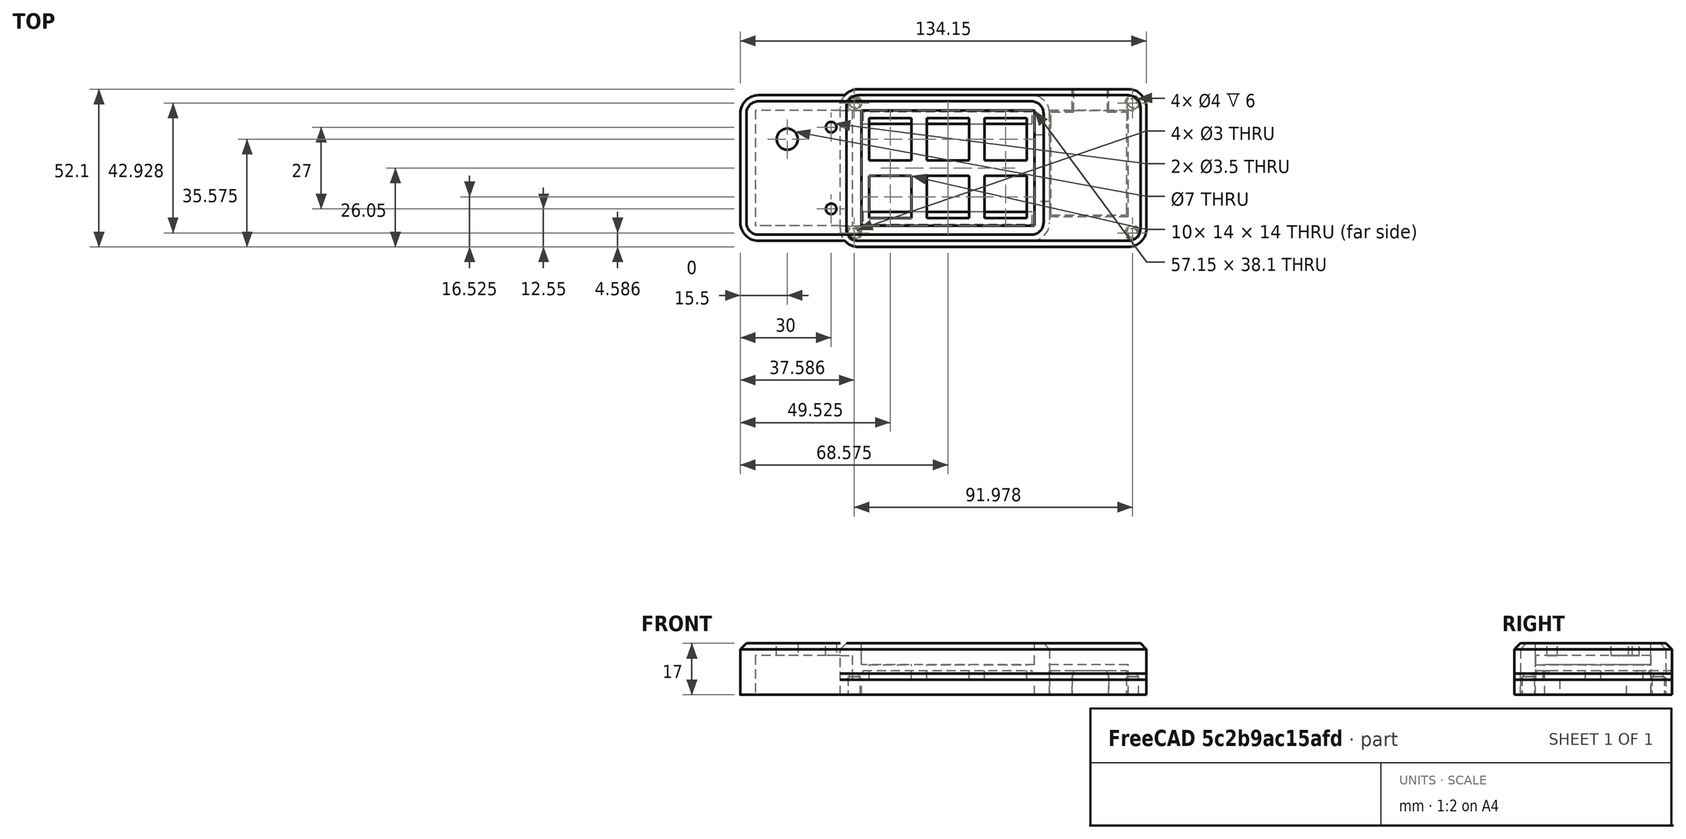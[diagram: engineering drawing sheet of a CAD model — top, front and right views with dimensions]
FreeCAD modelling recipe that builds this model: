
FCSTD DOCUMENT  (FreeCAD 0.21RUnknown)
Label: tm_keyb
License: All rights reserved
LicenseURL: https://en.wikipedia.org/wiki/All_rights_reserved
objects: Sketcher::SketchObject×18, TechDraw::DrawViewDimension×18, PartDesign::Pad×11, PartDesign::Pocket×9, TechDraw::DrawViewPart×6, PartDesign::Fillet×3, PartDesign::Chamfer×3, PartDesign::Body×3, PartDesign::ShapeBinder×1, Part::Mirroring×1, TechDraw::DrawSVGTemplate×1, TechDraw::DrawPage×1
note: 103 computed .brp shape members not serialized (recipe doc carries the construction recipe); baked Part::Feature solids carry a one-line shape summary decoded from their .brp

FEATURE [Sketcher::SketchObject] Sketch
  FullyConstrained = true
  MapMode = 5
  Support = -> [XY_Plane]
  sketch-geometry (45):
    g0: LineSegment StartX=-57.15 StartY=38.1 StartZ=0 EndX=0 EndY=38.1 EndZ=0
    g1: LineSegment StartX=0 StartY=38.1 StartZ=0 EndX=0 EndY=0 EndZ=0
    g2: LineSegment StartX=0 StartY=0 StartZ=0 EndX=-57.15 EndY=0 EndZ=0
    g3: LineSegment StartX=-57.15 StartY=0 StartZ=0 EndX=-57.15 EndY=38.1 EndZ=0
    g4: LineSegment StartX=-54.625 StartY=35.575 StartZ=0 EndX=-40.625 EndY=35.575 EndZ=0
    g5: LineSegment StartX=-40.625 StartY=35.575 StartZ=0 EndX=-40.625 EndY=21.575 EndZ=0
    g6: LineSegment StartX=-40.625 StartY=21.575 StartZ=0 EndX=-54.625 EndY=21.575 EndZ=0
    g7: LineSegment StartX=-54.625 StartY=21.575 StartZ=0 EndX=-54.625 EndY=35.575 EndZ=0
    g8: LineSegment StartX=-35.575 StartY=35.575 StartZ=0 EndX=-21.575 EndY=35.575 EndZ=0
    g9: LineSegment StartX=-21.575 StartY=35.575 StartZ=0 EndX=-21.575 EndY=21.575 EndZ=0
    g10: LineSegment StartX=-21.575 StartY=21.575 StartZ=0 EndX=-35.575 EndY=21.575 EndZ=0
    g11: LineSegment StartX=-35.575 StartY=21.575 StartZ=0 EndX=-35.575 EndY=35.575 EndZ=0
    g12: LineSegment StartX=-16.525 StartY=35.575 StartZ=0 EndX=-2.525 EndY=35.575 EndZ=0
    g13: LineSegment StartX=-2.525 StartY=35.575 StartZ=0 EndX=-2.525 EndY=21.575 EndZ=0
    g14: LineSegment StartX=-2.525 StartY=21.575 StartZ=0 EndX=-16.525 EndY=21.575 EndZ=0
    g15: LineSegment StartX=-16.525 StartY=21.575 StartZ=0 EndX=-16.525 EndY=35.575 EndZ=0
    g16: LineSegment StartX=-54.625 StartY=16.525 StartZ=0 EndX=-40.625 EndY=16.525 EndZ=0
    g17: LineSegment StartX=-40.625 StartY=16.525 StartZ=0 EndX=-40.625 EndY=2.525 EndZ=0
    g18: LineSegment StartX=-40.625 StartY=2.525 StartZ=0 EndX=-54.625 EndY=2.525 EndZ=0
    g19: LineSegment StartX=-54.625 StartY=2.525 StartZ=0 EndX=-54.625 EndY=16.525 EndZ=0
    g20: LineSegment StartX=-35.575 StartY=16.525 StartZ=0 EndX=-21.575 EndY=16.525 EndZ=0
    g21: LineSegment StartX=-21.575 StartY=16.525 StartZ=0 EndX=-21.575 EndY=2.525 EndZ=0
    g22: LineSegment StartX=-21.575 StartY=2.525 StartZ=0 EndX=-35.575 EndY=2.525 EndZ=0
    g23: LineSegment StartX=-35.575 StartY=2.525 StartZ=0 EndX=-35.575 EndY=16.525 EndZ=0
    g24: LineSegment StartX=-16.525 StartY=16.525 StartZ=0 EndX=-2.525 EndY=16.525 EndZ=0
    g25: LineSegment StartX=-2.525 StartY=16.525 StartZ=0 EndX=-2.525 EndY=2.525 EndZ=0
    g26: LineSegment StartX=-2.525 StartY=2.525 StartZ=0 EndX=-16.525 EndY=2.525 EndZ=0
    g27: LineSegment StartX=-16.525 StartY=2.525 StartZ=0 EndX=-16.525 EndY=16.525 EndZ=0
    g28: LineSegment StartX=0 StartY=38.1 StartZ=0 EndX=-19.05 EndY=38.1 EndZ=0
    g29: LineSegment StartX=-19.05 StartY=38.1 StartZ=0 EndX=-19.05 EndY=19.05 EndZ=0
    g30: LineSegment StartX=-19.05 StartY=19.05 StartZ=0 EndX=0 EndY=19.05 EndZ=0
    g31: LineSegment StartX=0 StartY=19.05 StartZ=0 EndX=0 EndY=38.1 EndZ=0
    g32: LineSegment StartX=-16.525 StartY=35.575 StartZ=0 EndX=-19.05 EndY=38.1 EndZ=0
    g33: LineSegment StartX=-2.525 StartY=35.575 StartZ=0 EndX=0 EndY=38.1 EndZ=0
    g34: LineSegment StartX=-2.525 StartY=21.575 StartZ=0 EndX=0 EndY=19.05 EndZ=0
    g35: LineSegment StartX=-16.525 StartY=21.575 StartZ=0 EndX=-19.05 EndY=19.05 EndZ=0
    g36: LineSegment StartX=-57.15 StartY=19.05 StartZ=0 EndX=-38.1 EndY=19.05 EndZ=0
    g37: LineSegment StartX=-38.1 StartY=19.05 StartZ=0 EndX=-38.1 EndY=0 EndZ=0
    g38: LineSegment StartX=-38.1 StartY=0 StartZ=0 EndX=-57.15 EndY=0 EndZ=0
    g39: LineSegment StartX=-57.15 StartY=0 StartZ=0 EndX=-57.15 EndY=19.05 EndZ=0
    g40: LineSegment StartX=-19.05 StartY=19.05 StartZ=0 EndX=0 EndY=19.05 EndZ=0
    g41: LineSegment StartX=0 StartY=19.05 StartZ=0 EndX=0 EndY=0 EndZ=0
    g42: LineSegment StartX=0 StartY=0 StartZ=0 EndX=-19.05 EndY=0 EndZ=0
    g43: LineSegment StartX=-19.05 StartY=0 StartZ=0 EndX=-19.05 EndY=19.05 EndZ=0
    g44: LineSegment StartX=-38.1 StartY=19.05 StartZ=0 EndX=-19.05 EndY=19.05 EndZ=0
  constraints (126):
    c: Coincident(g0,g1)
    c: Coincident(g1,g2)
    c: Coincident(g2,g3)
    c: Coincident(g3,g0)
    c: Horizontal(g0)
    c: Horizontal(g2)
    c: Vertical(g1)
    c: Vertical(g3)
    c: Coincident(g1,g-1)
    c: Coincident(g4,g5)
    c: Coincident(g5,g6)
    c: Coincident(g6,g7)
    c: Coincident(g7,g4)
    c: Horizontal(g4)
    c: Horizontal(g6)
    c: Vertical(g5)
    c: Vertical(g7)
    c: Coincident(g8,g9)
    c: Coincident(g9,g10)
    c: Coincident(g10,g11)
    c: Coincident(g11,g8)
    c: Horizontal(g8)
    c: Horizontal(g10)
    c: Vertical(g9)
    c: Vertical(g11)
    c: Coincident(g12,g13)
    c: Coincident(g13,g14)
    c: Coincident(g14,g15)
    c: Coincident(g15,g12)
    c: Horizontal(g12)
    c: Horizontal(g14)
    c: Vertical(g13)
    c: Vertical(g15)
    c: Coincident(g16,g17)
    c: Coincident(g17,g18)
    c: Coincident(g18,g19)
    c: Coincident(g19,g16)
    c: Horizontal(g16)
    c: Horizontal(g18)
    c: Vertical(g17)
    c: Vertical(g19)
    c: Coincident(g20,g21)
    c: Coincident(g21,g22)
    c: Coincident(g22,g23)
    c: Coincident(g23,g20)
    c: Horizontal(g20)
    c: Horizontal(g22)
    c: Vertical(g21)
    c: Vertical(g23)
    c: Coincident(g24,g25)
    c: Coincident(g25,g26)
    c: Coincident(g26,g27)
    c: Coincident(g27,g24)
    c: Horizontal(g24)
    c: Horizontal(g26)
    c: Vertical(g25)
    c: Vertical(g27)
    c: Horizontal(g10,g5)
    c: Horizontal(g5,g14)
    c: Horizontal(g16,g20)
    c: Horizontal(g20,g24)
    c: Vertical(g20,g10)
    c: Vertical(g5,g16)
    c: Vertical(g24,g14)
    c: Equal(g15,g12)
    c: Equal(g12,g8)
    c: Equal(g8,g9)
    c: Equal(g9,g4)
    c: Equal(g4,g5)
    c: Equal(g5,g16)
    c: Equal(g16,g17)
    c: Equal(g17,g24)
    c: Equal(g24,g27)
    c: Equal(g27,g21)
    c: Equal(g21,g20)
    c: DistanceX(g4,g4) = 14
    c: DistanceX(g4,g8) = 5.05
    c: DistanceX(g8,g12) = 5.05
    c: DistanceY(g24,g13) = 5.05
    c: Coincident(g28,g29)
    c: Coincident(g29,g30)
    c: Coincident(g30,g31)
    c: Coincident(g31,g28)
    c: Horizontal(g28)
    c: Horizontal(g30)
    c: Vertical(g29)
    c: Vertical(g31)
    c: Equal(g28,g31)
    c: DistanceY(g31,g31) = 19.05
    c: Coincident(g32,g12)
    c: Coincident(g32,g28)
    c: Coincident(g33,g12)
    c: Coincident(g33,g28)
    c: Coincident(g34,g13)
    c: Coincident(g34,g30)
    c: Coincident(g35,g14)
    c: Coincident(g35,g29)
    c: Equal(g35,g34)
    c: Equal(g34,g33)
    c: Vertical(g30,g1)
    c: Coincident(g36,g37)
    c: Coincident(g37,g38)
    c: Coincident(g38,g39)
    c: Coincident(g39,g36)
    c: Horizontal(g36)
    c: Horizontal(g38)
    c: Vertical(g37)
    c: Vertical(g39)
    c: PointOnObject(g37,g2)
    c: Coincident(g40,g41)
    c: Coincident(g41,g42)
    c: Coincident(g42,g43)
    c: Coincident(g43,g40)
    c: Horizontal(g42)
    c: Vertical(g43)
    c: Coincident(g40,g29)
    c: Coincident(g40,g30)
    c: Coincident(g41,g1)
    c: Equal(g29,g43)
    c: Equal(g43,g36)
    c: Equal(g36,g37)
    c: Coincident(g44,g36)
    c: Coincident(g44,g29)
    c: Equal(g44,g36)
    c: Vertical(g36,g0)
    c: Horizontal(g0,g28)
FEATURE [PartDesign::Pad] Pad
  Direction = (0,0,1)
  Length = 5
  Length2 = 10
  Profile = -> Sketch
  ReferenceAxis = -> Sketch [N_Axis]
  Type = 0
FEATURE [Sketcher::SketchObject] Sketch001
  ExternalGeometry = -> [Pad]
  FullyConstrained = true
  MapMode = 5
  Support = -> [XY_Plane]
  sketch-geometry (8):
    g0: LineSegment StartX=-64.15 StartY=45.1 StartZ=0 EndX=7 EndY=45.1 EndZ=0
    g1: LineSegment StartX=7 StartY=45.1 StartZ=0 EndX=7 EndY=-7 EndZ=0
    g2: LineSegment StartX=7 StartY=-7 StartZ=0 EndX=-64.15 EndY=-7 EndZ=0
    g3: LineSegment StartX=-64.15 StartY=-7 StartZ=0 EndX=-64.15 EndY=45.1 EndZ=0
    g4: LineSegment StartX=-57.15 StartY=38.1 StartZ=0 EndX=0 EndY=38.1 EndZ=0
    g5: LineSegment StartX=0 StartY=38.1 StartZ=0 EndX=0 EndY=0 EndZ=0
    g6: LineSegment StartX=0 StartY=0 StartZ=0 EndX=-57.15 EndY=0 EndZ=0
    g7: LineSegment StartX=-57.15 StartY=0 StartZ=0 EndX=-57.15 EndY=38.1 EndZ=0
  constraints (22):
    c: Coincident(g0,g1)
    c: Coincident(g1,g2)
    c: Coincident(g2,g3)
    c: Coincident(g3,g0)
    c: Horizontal(g0)
    c: Horizontal(g2)
    c: Vertical(g1)
    c: Vertical(g3)
    c: Coincident(g4,g5)
    c: Coincident(g5,g6)
    c: Coincident(g6,g7)
    c: Coincident(g7,g4)
    c: Horizontal(g4)
    c: Horizontal(g6)
    c: Vertical(g5)
    c: Vertical(g7)
    c: Coincident(g5,g-1)
    c: Coincident(g4,g-3)
    c: DistanceX(g0,g4) = 7
    c: DistanceX(g4,g0) = 7
    c: DistanceY(g1,g5) = 7
    c: DistanceY(g4,g0) = 7
FEATURE [PartDesign::Pad] Pad001
  BaseFeature = -> Pad
  Direction = (0,0,1)
  Length = 12
  Length2 = 5
  Profile = -> Sketch001
  ReferenceAxis = -> Sketch001 [N_Axis]
  Type = 4
  expr: Length = 5 + 7
FEATURE [Sketcher::SketchObject] Sketch002
  ExternalGeometry = -> [Pad001]
  FullyConstrained = true
  MapMode = 5
  Placement = pos=(-64.15,0,0) rot=(0.57735,-0.57735,-0.57735;2.0944rad)
  Support = -> [Pad001]
  sketch-geometry (4):
    g0: LineSegment StartX=-45.1 StartY=12 StartZ=0 EndX=7 EndY=12 EndZ=0
    g1: LineSegment StartX=7 StartY=12 StartZ=0 EndX=7 EndY=8 EndZ=0
    g2: LineSegment StartX=7 StartY=8 StartZ=0 EndX=-45.1 EndY=8 EndZ=0
    g3: LineSegment StartX=-45.1 StartY=8 StartZ=0 EndX=-45.1 EndY=12 EndZ=0
  constraints (10):
    c: Coincident(g0,g1)
    c: Coincident(g1,g2)
    c: Coincident(g2,g3)
    c: Coincident(g3,g0)
    c: Horizontal(g2)
    c: Vertical(g1)
    c: Vertical(g3)
    c: Coincident(g-3,g0)
    c: Coincident(g0,g-3)
    c: DistanceY(g1,g1) = 4
FEATURE [PartDesign::Pad] Pad002
  BaseFeature = -> Pad001
  Direction = (-1,0,0)
  Length = 35
  Length2 = 10
  Profile = -> Sketch002
  ReferenceAxis = -> Sketch002 [N_Axis]
  Type = 0
FEATURE [Sketcher::SketchObject] Sketch003
  ExternalGeometry = -> [Pad002]
  FullyConstrained = true
  MapMode = 5
  Placement = pos=(0,0,12) rot=(0,0,1;0rad)
  Support = -> [Pad002]
  sketch-geometry (5):
    g0: Circle CenterX=-81.65 CenterY=28.575 CenterZ=0 NormalX=0 NormalY=0 NormalZ=1 AngleXU=0 Radius=3.5
    g1: LineSegment StartX=-99.15 StartY=45.1 StartZ=0 EndX=-81.65 EndY=28.575 EndZ=0
    g2: LineSegment StartX=-81.65 StartY=28.575 StartZ=0 EndX=-64.15 EndY=45.1 EndZ=0
    g3: LineSegment StartX=-81.65 StartY=28.575 StartZ=0 EndX=-54.625 EndY=35.575 EndZ=0
    g4: LineSegment StartX=-81.65 StartY=28.575 StartZ=0 EndX=-54.625 EndY=21.575 EndZ=0
  constraints (11):
    c: Diameter(g0) = 7
    c: Coincident(g1,g-3)
    c: Coincident(g1,g0)
    c: Coincident(g2,g0)
    c: Coincident(g2,g-4)
    c: Equal(g2,g1)
    c: Coincident(g3,g0)
    c: Coincident(g3,g-5)
    c: Coincident(g4,g0)
    c: Coincident(g4,g-5)
    c: Equal(g3,g4)
FEATURE [PartDesign::Pocket] Pocket
  BaseFeature = -> Pad002
  Direction = (0,0,-1)
  Length = 5
  Length2 = 5
  Profile = -> Sketch003
  ReferenceAxis = -> Sketch003 [N_Axis]
  Type = 1
FEATURE [Sketcher::SketchObject] Sketch004
  ExternalGeometry = -> [Pocket]
  FullyConstrained = true
  MapMode = 5
  Placement = pos=(-64.15,0,0) rot=(0.57735,-0.57735,-0.57735;2.0944rad)
  Support = -> [Pocket]
  sketch-geometry (4):
    g0: LineSegment StartX=-38.1 StartY=-5 StartZ=0 EndX=0 EndY=-5 EndZ=0
    g1: LineSegment StartX=0 StartY=-5 StartZ=0 EndX=0 EndY=8 EndZ=0
    g2: LineSegment StartX=0 StartY=8 StartZ=0 EndX=-38.1 EndY=8 EndZ=0
    g3: LineSegment StartX=-38.1 StartY=8 StartZ=0 EndX=-38.1 EndY=-5 EndZ=0
  constraints (10):
    c: Coincident(g0,g1)
    c: Coincident(g1,g2)
    c: Coincident(g2,g3)
    c: Coincident(g3,g0)
    c: Horizontal(g2)
    c: Vertical(g1)
    c: Vertical(g3)
    c: Coincident(g0,g-3)
    c: PointOnObject(g1,g-5)
    c: Coincident(g0,g-4)
FEATURE [PartDesign::Pocket] Pocket001
  BaseFeature = -> Pocket
  Direction = (1,0,0)
  Length = 7
  Length2 = 5
  Profile = -> Sketch004
  ReferenceAxis = -> Sketch004 [N_Axis]
  Type = 0
FEATURE [PartDesign::Pad] Pad003
  BaseFeature = -> Pocket001
  Direction = (-1,0,0)
  Length = 10
  Length2 = 10
  Profile = -> Pocket001 [Face2,Face12]
  Type = 3
  UpToFace = -> Pocket001 [Face10]
FEATURE [Sketcher::SketchObject] Sketch005
  ExternalGeometry = -> [Pad003]
  FullyConstrained = true
  MapMode = 5
  Placement = pos=(0,38.1,0) rot=(1,0,0;1.5708rad)
  Support = -> [Pad003]
  sketch-geometry (4):
    g0: LineSegment StartX=-99.15 StartY=8 StartZ=0 EndX=-92.15 EndY=8 EndZ=0
    g1: LineSegment StartX=-92.15 StartY=8 StartZ=0 EndX=-92.15 EndY=-5 EndZ=0
    g2: LineSegment StartX=-92.15 StartY=-5 StartZ=0 EndX=-99.15 EndY=-5 EndZ=0
    g3: LineSegment StartX=-99.15 StartY=-5 StartZ=0 EndX=-99.15 EndY=8 EndZ=0
  constraints (10):
    c: Coincident(g0,g1)
    c: Coincident(g1,g2)
    c: Coincident(g2,g3)
    c: Coincident(g3,g0)
    c: Horizontal(g0)
    c: Horizontal(g2)
    c: Vertical(g1)
    c: DistanceX(g2,g2) = 7
    c: Coincident(g2,g-4)
    c: Coincident(g0,g-3)
FEATURE [PartDesign::Pad] Pad004
  BaseFeature = -> Pad003
  Direction = (0,-1,2e-16)
  Length = 31
  Length2 = 10
  Profile = -> Sketch005
  ReferenceAxis = -> Sketch005 [N_Axis]
  Type = 1
FEATURE [Sketcher::SketchObject] Sketch006
  ExternalGeometry = -> [Pad004]
  FullyConstrained = true
  MapMode = 5
  Placement = pos=(0,0,12) rot=(0,0,1;0rad)
  Support = -> [Pad004]
  sketch-geometry (8):
    g0: LineSegment StartX=-99.15 StartY=45.1 StartZ=0 EndX=7 EndY=45.1 EndZ=0
    g1: LineSegment StartX=7 StartY=45.1 StartZ=0 EndX=7 EndY=-7 EndZ=0
    g2: LineSegment StartX=7 StartY=-7 StartZ=0 EndX=-99.15 EndY=-7 EndZ=0
    g3: LineSegment StartX=-99.15 StartY=-7 StartZ=0 EndX=-99.15 EndY=45.1 EndZ=0
    g4: LineSegment StartX=-97.15 StartY=43.1 StartZ=0 EndX=5 EndY=43.1 EndZ=0
    g5: LineSegment StartX=5 StartY=43.1 StartZ=0 EndX=5 EndY=-5 EndZ=0
    g6: LineSegment StartX=5 StartY=-5 StartZ=0 EndX=-97.15 EndY=-5 EndZ=0
    g7: LineSegment StartX=-97.15 StartY=-5 StartZ=0 EndX=-97.15 EndY=43.1 EndZ=0
  constraints (22):
    c: Coincident(g0,g1)
    c: Coincident(g1,g2)
    c: Coincident(g2,g3)
    c: Coincident(g3,g0)
    c: Horizontal(g0)
    c: Horizontal(g2)
    c: Vertical(g1)
    c: Vertical(g3)
    c: Coincident(g0,g-4)
    c: Coincident(g1,g-3)
    c: Coincident(g4,g5)
    c: Coincident(g5,g6)
    c: Coincident(g6,g7)
    c: Coincident(g7,g4)
    c: Horizontal(g4)
    c: Horizontal(g6)
    c: Vertical(g5)
    c: Vertical(g7)
    c: DistanceY(g4,g0) = 2
    c: DistanceX(g4,g0) = 2
    c: DistanceY(g1,g5) = 2
    c: DistanceX(g2,g6) = 2
FEATURE [PartDesign::Pocket] Pocket002
  BaseFeature = -> Pad004
  Direction = (0,0,-1)
  Length = 5
  Length2 = 5
  Profile = -> Sketch006
  ReferenceAxis = -> Sketch006 [N_Axis]
  Type = 1
FEATURE [PartDesign::Fillet] Fillet
  Base = -> Pocket002 [Edge15,Edge20,Edge17,Edge13]
  BaseFeature = -> Pocket002
  Radius = 6
  SupportTransform = false
  UseAllEdges = false
FEATURE [Sketcher::SketchObject] Sketch007
  ExternalGeometry = -> [Fillet]
  FullyConstrained = true
  MapMode = 5
  Placement = pos=(0,0,12) rot=(0,0,1;0rad)
  Support = -> [Fillet]
  sketch-geometry (4):
    g0: Circle CenterX=-67.15 CenterY=5.55 CenterZ=0 NormalX=0 NormalY=0 NormalZ=1 AngleXU=0 Radius=1.75
    g1: Circle CenterX=-67.15 CenterY=32.55 CenterZ=0 NormalX=0 NormalY=0 NormalZ=1 AngleXU=0 Radius=1.75
    g2: LineSegment StartX=-67.15 StartY=32.55 StartZ=0 EndX=-64.15 EndY=43.1 EndZ=0
    g3: LineSegment StartX=-67.15 StartY=5.55 StartZ=0 EndX=-64.15 EndY=-5 EndZ=0
  constraints (10):
    c: Equal(g0,g1)
    c: Vertical(g0,g1)
    c: Diameter(g1) = 3.5
    c: Coincident(g2,g1)
    c: Coincident(g2,g-3)
    c: Coincident(g3,g0)
    c: Coincident(g3,g-3)
    c: Equal(g2,g3)
    c: DistanceX(g1,g2) = 3
    c: DistanceY(g0,g1) = 27
FEATURE [PartDesign::Pocket] Pocket003
  BaseFeature = -> Fillet
  Direction = (0,0,-1)
  Length = 5
  Length2 = 5
  Profile = -> Sketch007
  ReferenceAxis = -> Sketch007 [N_Axis]
  Type = 1
FEATURE [Sketcher::SketchObject] Sketch008
  ExternalGeometry = -> [Pocket003]
  FullyConstrained = true
  MapMode = 5
  Placement = pos=(0,0,8) rot=(1,0,0;3.14159rad)
  Support = -> [Pocket003]
  sketch-geometry (4):
    g0: LineSegment StartX=-57.15 StartY=0 StartZ=0 EndX=-60.15 EndY=0 EndZ=0
    g1: LineSegment StartX=-60.15 StartY=0 StartZ=0 EndX=-60.15 EndY=-38.1 EndZ=0
    g2: LineSegment StartX=-60.15 StartY=-38.1 StartZ=0 EndX=-57.15 EndY=-38.1 EndZ=0
    g3: LineSegment StartX=-57.15 StartY=-38.1 StartZ=0 EndX=-57.15 EndY=0 EndZ=0
  constraints (10):
    c: Coincident(g0,g1)
    c: Coincident(g1,g2)
    c: Coincident(g2,g3)
    c: Coincident(g3,g0)
    c: Horizontal(g0)
    c: Horizontal(g2)
    c: Vertical(g1)
    c: Coincident(g0,g-3)
    c: Coincident(g2,g-3)
    c: DistanceX(g2,g2) = 3
FEATURE [PartDesign::Pad] Pad005
  BaseFeature = -> Pocket003
  Direction = (0,0,-1)
  Length = 10
  Length2 = 10
  Profile = -> Sketch008
  ReferenceAxis = -> Sketch008 [N_Axis]
  Type = 3
  UpToFace = -> Pocket003 [Face22]
FEATURE [Sketcher::SketchObject] Sketch010
  ExternalGeometry = -> [Pad005]
  FullyConstrained = true
  MapMode = 5
  Placement = pos=(0,0,0) rot=(0,0.707107,0.707107;3.14159rad)
  Support = -> [Pad005]
  expr: Constraints[11] = 19 / 2
  sketch-geometry (5):
    g0: LineSegment StartX=77.65 StartY=2 StartZ=0 EndX=87.65 EndY=2 EndZ=0
    g1: LineSegment StartX=87.65 StartY=2 StartZ=0 EndX=87.65 EndY=-5 EndZ=0
    g2: LineSegment StartX=87.65 StartY=-5 StartZ=0 EndX=77.65 EndY=-5 EndZ=0
    g3: LineSegment StartX=77.65 StartY=-5 StartZ=0 EndX=77.65 EndY=2 EndZ=0
    g4: GeomPoint X=82.65 Y=-5 Z=0
  constraints (13):
    c: Coincident(g0,g1)
    c: Coincident(g1,g2)
    c: Coincident(g2,g3)
    c: Coincident(g3,g0)
    c: Horizontal(g0)
    c: Horizontal(g2)
    c: Vertical(g1)
    c: Vertical(g3)
    c: Horizontal(g2,g-3)
    c: DistanceX(g0,g0) = 10
    c: Symmetric(g1,g2,g4)
    c: DistanceX(g4,g-3) = 9.5
    c: DistanceY(g3,g3) = 7
FEATURE [PartDesign::Pocket] Pocket004
  BaseFeature = -> Pad005
  Direction = (0,-1,2e-16)
  Length = 5
  Length2 = 5
  Profile = -> Sketch010
  ReferenceAxis = -> Sketch010 [N_Axis]
  Type = 0
FEATURE [PartDesign::Chamfer] Chamfer
  Angle = 45
  Base = -> Pocket004 [Edge13]
  BaseFeature = -> Pocket004
  ChamferType = 0
  FlipDirection = false
  Size = 2
  Size2 = 1
  SupportTransform = false
  UseAllEdges = false
FEATURE [PartDesign::Pad] Pad006
  BaseFeature = -> Chamfer
  Direction = (0,-2e-16,-1)
  Length = 10
  Length2 = 10
  Profile = -> Chamfer [Face46]
  Type = 3
  UpToFace = -> Chamfer [Face27]
FEATURE [PartDesign::Body] Body
  Group = -> [Sketch,Pad,Sketch001,Pad001,Sketch002,Pad002,Sketch003,Pocket,Sketch004,Pocket001,Pad003,Sketch005,Pad004,Sketch006,Pocket002,Fillet,Sketch007,Pocket003,Sketch008,Pad005,Sketch010,Pocket004,Chamfer,Pad006]
  Origin = -> Origin
  Tip = -> Pad006
FEATURE [Sketcher::SketchObject] Sketch011
  FullyConstrained = true
  MapMode = 5
  Support = -> [XY_Plane001]
  sketch-geometry (45):
    g0: LineSegment StartX=-57.15 StartY=38.1 StartZ=0 EndX=0 EndY=38.1 EndZ=0
    g1: LineSegment StartX=0 StartY=38.1 StartZ=0 EndX=0 EndY=0 EndZ=0
    g2: LineSegment StartX=0 StartY=0 StartZ=0 EndX=-57.15 EndY=0 EndZ=0
    g3: LineSegment StartX=-57.15 StartY=0 StartZ=0 EndX=-57.15 EndY=38.1 EndZ=0
    g4: LineSegment StartX=-54.625 StartY=35.575 StartZ=0 EndX=-40.625 EndY=35.575 EndZ=0
    g5: LineSegment StartX=-40.625 StartY=35.575 StartZ=0 EndX=-40.625 EndY=21.575 EndZ=0
    g6: LineSegment StartX=-40.625 StartY=21.575 StartZ=0 EndX=-54.625 EndY=21.575 EndZ=0
    g7: LineSegment StartX=-54.625 StartY=21.575 StartZ=0 EndX=-54.625 EndY=35.575 EndZ=0
    g8: LineSegment StartX=-35.575 StartY=35.575 StartZ=0 EndX=-21.575 EndY=35.575 EndZ=0
    g9: LineSegment StartX=-21.575 StartY=35.575 StartZ=0 EndX=-21.575 EndY=21.575 EndZ=0
    g10: LineSegment StartX=-21.575 StartY=21.575 StartZ=0 EndX=-35.575 EndY=21.575 EndZ=0
    g11: LineSegment StartX=-35.575 StartY=21.575 StartZ=0 EndX=-35.575 EndY=35.575 EndZ=0
    g12: LineSegment StartX=-16.525 StartY=35.575 StartZ=0 EndX=-2.525 EndY=35.575 EndZ=0
    g13: LineSegment StartX=-2.525 StartY=35.575 StartZ=0 EndX=-2.525 EndY=21.575 EndZ=0
    g14: LineSegment StartX=-2.525 StartY=21.575 StartZ=0 EndX=-16.525 EndY=21.575 EndZ=0
    g15: LineSegment StartX=-16.525 StartY=21.575 StartZ=0 EndX=-16.525 EndY=35.575 EndZ=0
    g16: LineSegment StartX=-54.625 StartY=16.525 StartZ=0 EndX=-40.625 EndY=16.525 EndZ=0
    g17: LineSegment StartX=-40.625 StartY=16.525 StartZ=0 EndX=-40.625 EndY=2.525 EndZ=0
    g18: LineSegment StartX=-40.625 StartY=2.525 StartZ=0 EndX=-54.625 EndY=2.525 EndZ=0
    g19: LineSegment StartX=-54.625 StartY=2.525 StartZ=0 EndX=-54.625 EndY=16.525 EndZ=0
    g20: LineSegment StartX=-35.575 StartY=16.525 StartZ=0 EndX=-21.575 EndY=16.525 EndZ=0
    g21: LineSegment StartX=-21.575 StartY=16.525 StartZ=0 EndX=-21.575 EndY=2.525 EndZ=0
    g22: LineSegment StartX=-21.575 StartY=2.525 StartZ=0 EndX=-35.575 EndY=2.525 EndZ=0
    g23: LineSegment StartX=-35.575 StartY=2.525 StartZ=0 EndX=-35.575 EndY=16.525 EndZ=0
    g24: LineSegment StartX=-16.525 StartY=16.525 StartZ=0 EndX=-2.525 EndY=16.525 EndZ=0
    g25: LineSegment StartX=-2.525 StartY=16.525 StartZ=0 EndX=-2.525 EndY=2.525 EndZ=0
    g26: LineSegment StartX=-2.525 StartY=2.525 StartZ=0 EndX=-16.525 EndY=2.525 EndZ=0
    g27: LineSegment StartX=-16.525 StartY=2.525 StartZ=0 EndX=-16.525 EndY=16.525 EndZ=0
    g28: LineSegment StartX=0 StartY=38.1 StartZ=0 EndX=-19.05 EndY=38.1 EndZ=0
    g29: LineSegment StartX=-19.05 StartY=38.1 StartZ=0 EndX=-19.05 EndY=19.05 EndZ=0
    g30: LineSegment StartX=-19.05 StartY=19.05 StartZ=0 EndX=0 EndY=19.05 EndZ=0
    g31: LineSegment StartX=0 StartY=19.05 StartZ=0 EndX=0 EndY=38.1 EndZ=0
    g32: LineSegment StartX=-16.525 StartY=35.575 StartZ=0 EndX=-19.05 EndY=38.1 EndZ=0
    g33: LineSegment StartX=-2.525 StartY=35.575 StartZ=0 EndX=0 EndY=38.1 EndZ=0
    g34: LineSegment StartX=-2.525 StartY=21.575 StartZ=0 EndX=0 EndY=19.05 EndZ=0
    g35: LineSegment StartX=-16.525 StartY=21.575 StartZ=0 EndX=-19.05 EndY=19.05 EndZ=0
    g36: LineSegment StartX=-57.15 StartY=19.05 StartZ=0 EndX=-38.1 EndY=19.05 EndZ=0
    g37: LineSegment StartX=-38.1 StartY=19.05 StartZ=0 EndX=-38.1 EndY=0 EndZ=0
    g38: LineSegment StartX=-38.1 StartY=0 StartZ=0 EndX=-57.15 EndY=0 EndZ=0
    g39: LineSegment StartX=-57.15 StartY=0 StartZ=0 EndX=-57.15 EndY=19.05 EndZ=0
    g40: LineSegment StartX=-19.05 StartY=19.05 StartZ=0 EndX=0 EndY=19.05 EndZ=0
    g41: LineSegment StartX=0 StartY=19.05 StartZ=0 EndX=0 EndY=0 EndZ=0
    g42: LineSegment StartX=0 StartY=0 StartZ=0 EndX=-19.05 EndY=0 EndZ=0
    g43: LineSegment StartX=-19.05 StartY=0 StartZ=0 EndX=-19.05 EndY=19.05 EndZ=0
    g44: LineSegment StartX=-38.1 StartY=19.05 StartZ=0 EndX=-19.05 EndY=19.05 EndZ=0
  constraints (126):
    c: Coincident(g0,g1)
    c: Coincident(g1,g2)
    c: Coincident(g2,g3)
    c: Coincident(g3,g0)
    c: Horizontal(g0)
    c: Horizontal(g2)
    c: Vertical(g1)
    c: Vertical(g3)
    c: Coincident(g1,g-1)
    c: Coincident(g4,g5)
    c: Coincident(g5,g6)
    c: Coincident(g6,g7)
    c: Coincident(g7,g4)
    c: Horizontal(g4)
    c: Horizontal(g6)
    c: Vertical(g5)
    c: Vertical(g7)
    c: Coincident(g8,g9)
    c: Coincident(g9,g10)
    c: Coincident(g10,g11)
    c: Coincident(g11,g8)
    c: Horizontal(g8)
    c: Horizontal(g10)
    c: Vertical(g9)
    c: Vertical(g11)
    c: Coincident(g12,g13)
    c: Coincident(g13,g14)
    c: Coincident(g14,g15)
    c: Coincident(g15,g12)
    c: Horizontal(g12)
    c: Horizontal(g14)
    c: Vertical(g13)
    c: Vertical(g15)
    c: Coincident(g16,g17)
    c: Coincident(g17,g18)
    c: Coincident(g18,g19)
    c: Coincident(g19,g16)
    c: Horizontal(g16)
    c: Horizontal(g18)
    c: Vertical(g17)
    c: Vertical(g19)
    c: Coincident(g20,g21)
    c: Coincident(g21,g22)
    c: Coincident(g22,g23)
    c: Coincident(g23,g20)
    c: Horizontal(g20)
    c: Horizontal(g22)
    c: Vertical(g21)
    c: Vertical(g23)
    c: Coincident(g24,g25)
    c: Coincident(g25,g26)
    c: Coincident(g26,g27)
    c: Coincident(g27,g24)
    c: Horizontal(g24)
    c: Horizontal(g26)
    c: Vertical(g25)
    c: Vertical(g27)
    c: Horizontal(g10,g5)
    c: Horizontal(g5,g14)
    c: Horizontal(g16,g20)
    c: Horizontal(g20,g24)
    c: Vertical(g20,g10)
    c: Vertical(g5,g16)
    c: Vertical(g24,g14)
    c: Equal(g15,g12)
    c: Equal(g12,g8)
    c: Equal(g8,g9)
    c: Equal(g9,g4)
    c: Equal(g4,g5)
    c: Equal(g5,g16)
    c: Equal(g16,g17)
    c: Equal(g17,g24)
    c: Equal(g24,g27)
    c: Equal(g27,g21)
    c: Equal(g21,g20)
    c: DistanceX(g4,g4) = 14
    c: DistanceX(g4,g8) = 5.05
    c: DistanceX(g8,g12) = 5.05
    c: DistanceY(g24,g13) = 5.05
    c: Coincident(g28,g29)
    c: Coincident(g29,g30)
    c: Coincident(g30,g31)
    c: Coincident(g31,g28)
    c: Horizontal(g28)
    c: Horizontal(g30)
    c: Vertical(g29)
    c: Vertical(g31)
    c: Equal(g28,g31)
    c: DistanceY(g31,g31) = 19.05
    c: Coincident(g32,g12)
    c: Coincident(g32,g28)
    c: Coincident(g33,g12)
    c: Coincident(g33,g28)
    c: Coincident(g34,g13)
    c: Coincident(g34,g30)
    c: Coincident(g35,g14)
    c: Coincident(g35,g29)
    c: Equal(g35,g34)
    c: Equal(g34,g33)
    c: Vertical(g30,g1)
    c: Coincident(g36,g37)
    c: Coincident(g37,g38)
    c: Coincident(g38,g39)
    c: Coincident(g39,g36)
    c: Horizontal(g36)
    c: Horizontal(g38)
    c: Vertical(g37)
    c: Vertical(g39)
    c: PointOnObject(g37,g2)
    c: Coincident(g40,g41)
    c: Coincident(g41,g42)
    c: Coincident(g42,g43)
    c: Coincident(g43,g40)
    c: Horizontal(g42)
    c: Vertical(g43)
    c: Coincident(g40,g29)
    c: Coincident(g40,g30)
    c: Coincident(g41,g1)
    c: Equal(g29,g43)
    c: Equal(g43,g36)
    c: Equal(g36,g37)
    c: Coincident(g44,g36)
    c: Coincident(g44,g29)
    c: Equal(g44,g36)
    c: Vertical(g36,g0)
    c: Horizontal(g0,g28)
FEATURE [PartDesign::Pad] Pad007
  Direction = (0,0,1)
  Length = 5
  Length2 = 10
  Profile = -> Sketch011
  ReferenceAxis = -> Sketch011 [N_Axis]
  Type = 0
FEATURE [Sketcher::SketchObject] Sketch012
  ExternalGeometry = -> [Pad007]
  FullyConstrained = true
  MapMode = 5
  Support = -> [XY_Plane001]
  expr: Constraints[23] = 8
  sketch-geometry (13):
    g0: LineSegment StartX=-64.15 StartY=45.1 StartZ=0 EndX=37 EndY=45.1 EndZ=0
    g1: LineSegment StartX=37 StartY=45.1 StartZ=0 EndX=37 EndY=-7 EndZ=0
    g2: LineSegment StartX=37 StartY=-7 StartZ=0 EndX=-64.15 EndY=-7 EndZ=0
    g3: LineSegment StartX=-64.15 StartY=-7 StartZ=0 EndX=-64.15 EndY=45.1 EndZ=0
    g4: LineSegment StartX=0 StartY=0 StartZ=0 EndX=-57.15 EndY=0 EndZ=0
    g5: LineSegment StartX=-57.15 StartY=0 StartZ=0 EndX=-57.15 EndY=38.1 EndZ=0
    g6: LineSegment StartX=8 StartY=38.1 StartZ=0 EndX=34 EndY=38.1 EndZ=0
    g7: LineSegment StartX=34 StartY=38.1 StartZ=0 EndX=34 EndY=0 EndZ=0
    g8: LineSegment StartX=34 StartY=0 StartZ=0 EndX=8 EndY=0 EndZ=0
    g9: LineSegment StartX=0 StartY=0 StartZ=0 EndX=8 EndY=0 EndZ=0
    g10: LineSegment StartX=-57.15 StartY=38.1 StartZ=0 EndX=0 EndY=38.1 EndZ=0
    g11: LineSegment StartX=0 StartY=38.1 StartZ=0 EndX=8 EndY=38.1 EndZ=0
    g12: LineSegment StartX=0 StartY=38.1 StartZ=0 EndX=0 EndY=0 EndZ=0
  constraints (35):
    c: Coincident(g0,g1)
    c: Coincident(g1,g2)
    c: Coincident(g2,g3)
    c: Coincident(g3,g0)
    c: Horizontal(g0)
    c: Horizontal(g2)
    c: Vertical(g1)
    c: Vertical(g3)
    c: Coincident(g4,g5)
    c: Horizontal(g4)
    c: Vertical(g5)
    c: DistanceX(g0,g5) = 7
    c: DistanceY(g1,g4) = 7
    c: DistanceY(g5,g0) = 7
    c: Coincident(g6,g7)
    c: Coincident(g7,g8)
    c: Horizontal(g6)
    c: Horizontal(g8)
    c: Vertical(g7)
    c: Horizontal(g8,g4)
    c: DistanceX(g6,g6) = 26
    c: Vertical(g6,g8)
    c: Coincident(g9,g8)
    c: DistanceX(g9,g9) = 8
    c: Coincident(g9,g4)
    c: Coincident(g4,g-1)
    c: Coincident(g10,g5)
    c: Coincident(g10,g-3)
    c: Coincident(g11,g10)
    c: Coincident(g11,g6)
    c: Horizontal(g11)
    c: Coincident(g5,g-3)
    c: DistanceX(g6,g0) = 3
    c: Coincident(g12,g10)
    c: Coincident(g12,g4)
FEATURE [PartDesign::Pad] Pad008
  BaseFeature = -> Pad007
  Direction = (0,0,1)
  Length = 12
  Length2 = 5
  Profile = -> Sketch012
  ReferenceAxis = -> Sketch012 [N_Axis]
  Type = 4
  expr: Length = 5 + 7
FEATURE [PartDesign::Fillet] Fillet001
  Base = -> Pad008 [Edge8,Edge2,Edge5,Edge1]
  BaseFeature = -> Pad008
  Radius = 6
  SupportTransform = false
  UseAllEdges = false
FEATURE [Sketcher::SketchObject] Sketch013
  ExternalGeometry = -> [Fillet001]
  FullyConstrained = true
  MapMode = 5
  Placement = pos=(0,0,-5) rot=(1,0,0;3.14159rad)
  Support = -> [Fillet001]
  sketch-geometry (16):
    g0: LineSegment StartX=5 StartY=0 StartZ=0 EndX=31 EndY=0 EndZ=0
    g1: LineSegment StartX=31 StartY=0 StartZ=0 EndX=31 EndY=-35 EndZ=0
    g2: LineSegment StartX=31 StartY=-35 StartZ=0 EndX=5 EndY=-35 EndZ=0
    g3: LineSegment StartX=5 StartY=-35 StartZ=0 EndX=5 EndY=0 EndZ=0
    g4: LineSegment StartX=0 StartY=-38.1 StartZ=0 EndX=31 EndY=-38.1 EndZ=0
    g5: LineSegment StartX=31 StartY=-38.1 StartZ=0 EndX=31 EndY=0 EndZ=0
    g6: LineSegment StartX=5 StartY=-8 StartZ=0 EndX=-2.525 EndY=-8 EndZ=0
    g7: LineSegment StartX=-2.525 StartY=-30.1 StartZ=0 EndX=5 EndY=-30.1 EndZ=0
    g8: LineSegment StartX=5 StartY=-30.1 StartZ=0 EndX=5 EndY=-38.1 EndZ=0
    g9: LineSegment StartX=5 StartY=-38.1 StartZ=0 EndX=31 EndY=-38.1 EndZ=0
    g10: LineSegment StartX=5 StartY=0 StartZ=0 EndX=5 EndY=-8 EndZ=0
    g11: LineSegment StartX=5 StartY=0 StartZ=0 EndX=31 EndY=0 EndZ=0
    g12: LineSegment StartX=-2.525 StartY=-30.1 StartZ=0 EndX=-2.525 EndY=-8 EndZ=0
    g13: LineSegment StartX=5 StartY=-3 StartZ=0 EndX=31 EndY=-3 EndZ=0
    g14: LineSegment StartX=5 StartY=-8 StartZ=0 EndX=5 EndY=-3 EndZ=0
    g15: LineSegment StartX=31 StartY=-3 StartZ=0 EndX=31 EndY=-38.1 EndZ=0
  constraints (44):
    c: Coincident(g0,g1)
    c: Coincident(g1,g2)
    c: Coincident(g2,g3)
    c: Coincident(g3,g0)
    c: Horizontal(g0)
    c: Horizontal(g2)
    c: Vertical(g1)
    c: Vertical(g3)
    c: DistanceY(g3,g3) = 35
    c: DistanceX(g0,g0) = 26
    c: Horizontal(g0,g-1)
    c: Vertical(g0,g-3)
    c: Coincident(g4,g5)
    c: Horizontal(g4)
    c: Vertical(g5)
    c: Coincident(g4,g-4)
    c: Horizontal(g7)
    c: PointOnObject(g8,g-4)
    c: Vertical(g8)
    c: Horizontal(g6)
    c: Coincident(g7,g8)
    c: Vertical(g6,g7)
    c: Coincident(g5,g0)
    c: Coincident(g9,g8)
    c: Coincident(g9,g5)
    c: Coincident(g10,g0)
    c: Coincident(g10,g6)
    c: Vertical(g10)
    c: DistanceY(g8,g8) = 8
    c: Equal(g10,g8)
    c: Vertical(g6,g-5)
    c: Coincident(g11,g10)
    c: Coincident(g11,g5)
    c: Coincident(g12,g7)
    c: Vertical(g12)
    c: Coincident(g12,g6)
    c: PointOnObject(g13,g10)
    c: PointOnObject(g13,g5)
    c: Horizontal(g13)
    c: DistanceY(g13,g5) = 3
    c: Coincident(g14,g6)
    c: Coincident(g14,g13)
    c: Coincident(g15,g13)
    c: Coincident(g15,g9)
FEATURE [PartDesign::Pocket] Pocket005
  BaseFeature = -> Fillet001
  Direction = (0,0,1)
  Length = 0
  Length2 = 5
  Profile = -> Sketch013
  ReferenceAxis = -> Sketch013 [N_Axis]
  Type = 3
  UpToFace = -> Fillet001 [Face19]
FEATURE [Sketcher::SketchObject] Sketch014
  ExternalGeometry = -> [Pocket005]
  FullyConstrained = true
  MapMode = 5
  Placement = pos=(0,0,0) rot=(1,0,0;3.14159rad)
  Support = -> [Pocket005]
  sketch-geometry (4):
    g0: LineSegment StartX=5 StartY=-3 StartZ=0 EndX=31 EndY=-3 EndZ=0
    g1: LineSegment StartX=31 StartY=-3 StartZ=0 EndX=31 EndY=-38.1 EndZ=0
    g2: LineSegment StartX=31 StartY=-38.1 StartZ=0 EndX=5 EndY=-38.1 EndZ=0
    g3: LineSegment StartX=5 StartY=-38.1 StartZ=0 EndX=5 EndY=-3 EndZ=0
  constraints (10):
    c: Coincident(g0,g1)
    c: Coincident(g1,g2)
    c: Coincident(g2,g3)
    c: Coincident(g3,g0)
    c: Horizontal(g0)
    c: Horizontal(g2)
    c: Vertical(g1)
    c: Vertical(g3)
    c: Coincident(g0,g-3)
    c: Coincident(g1,g-4)
FEATURE [PartDesign::Pocket] Pocket006
  BaseFeature = -> Pocket005
  Direction = (0,0,1)
  Length = 0
  Length2 = 5
  Profile = -> Sketch014
  ReferenceAxis = -> Sketch014 [N_Axis]
  Type = 3
  UpToFace = -> Pocket005 [Face29]
FEATURE [Sketcher::SketchObject] Sketch015
  ExternalGeometry = -> [Pocket006]
  FullyConstrained = true
  MapMode = 5
  Placement = pos=(0,38.1,0) rot=(1,0,0;1.5708rad)
  Support = -> [Pocket006]
  sketch-geometry (5):
    g0: LineSegment StartX=12.5 StartY=2 StartZ=0 EndX=24.5 EndY=2 EndZ=0
    g1: LineSegment StartX=24.5 StartY=2 StartZ=0 EndX=24.5 EndY=-5 EndZ=0
    g2: LineSegment StartX=24.5 StartY=-5 StartZ=0 EndX=12.5 EndY=-5 EndZ=0
    g3: LineSegment StartX=12.5 StartY=-5 StartZ=0 EndX=12.5 EndY=2 EndZ=0
    g4: LineSegment StartX=12.5 StartY=-5 StartZ=0 EndX=5 EndY=-5 EndZ=0
  constraints (15):
    c: Coincident(g0,g1)
    c: Coincident(g1,g2)
    c: Coincident(g2,g3)
    c: Coincident(g3,g0)
    c: Horizontal(g0)
    c: Horizontal(g2)
    c: Vertical(g1)
    c: Vertical(g3)
    c: DistanceX(g1,g-3) = 6.5
    c: Coincident(g4,g2)
    c: Horizontal(g4)
    c: DistanceX(g4,g-3) = 26
    c: PointOnObject(g1,g-3)
    c: DistanceY(g1,g1) = 7
    c: DistanceX(g0,g0) = 12
FEATURE [PartDesign::Pocket] Pocket007
  BaseFeature = -> Pocket006
  Direction = (0,1,-2e-16)
  Length = 5
  Length2 = 5
  Profile = -> Sketch015
  ReferenceAxis = -> Sketch015 [N_Axis]
  Type = 1
FEATURE [PartDesign::Fillet] Fillet002
  Base = -> Pocket007 [Edge35,Edge33]
  BaseFeature = -> Pocket007
  Radius = 1
  SupportTransform = false
  UseAllEdges = false
FEATURE [PartDesign::Chamfer] Chamfer001
  Angle = 45
  Base = -> Fillet002 [Edge49]
  BaseFeature = -> Fillet002
  ChamferType = 0
  FlipDirection = false
  Size = 2
  Size2 = 1
  SupportTransform = false
  UseAllEdges = false
FEATURE [Sketcher::SketchObject] Sketch018
  ExternalGeometry = -> [Chamfer001]
  FullyConstrained = true
  MapMode = 5
  Placement = pos=(0,0,-5) rot=(1,0,0;3.14159rad)
  Support = -> [Chamfer001]
  sketch-geometry (18):
    g0: LineSegment StartX=-60.9784 StartY=3.82843 StartZ=0 EndX=33.8284 EndY=3.82843 EndZ=0
    g1: LineSegment StartX=33.8284 StartY=3.82843 StartZ=0 EndX=33.8284 EndY=-41.9284 EndZ=0
    g2: LineSegment StartX=33.8284 StartY=-41.9284 StartZ=0 EndX=-60.9784 EndY=-41.9284 EndZ=0
    g3: LineSegment StartX=-60.9784 StartY=-41.9284 StartZ=0 EndX=-60.9784 EndY=3.82843 EndZ=0
    g4: LineSegment StartX=-58.15 StartY=1 StartZ=0 EndX=-60.9784 EndY=3.82843 EndZ=0
    g5: LineSegment StartX=31 StartY=1 StartZ=0 EndX=33.8284 EndY=3.82843 EndZ=0
    g6: LineSegment StartX=33.8284 StartY=-41.9284 StartZ=0 EndX=35.2426 EndY=-43.3426 EndZ=0
    g7: LineSegment StartX=33.8284 StartY=-41.9284 StartZ=0 EndX=31 EndY=-39.1 EndZ=0
    g8: LineSegment StartX=33.8284 StartY=3.82843 StartZ=0 EndX=35.2426 EndY=5.24264 EndZ=0
    g9: LineSegment StartX=-60.9784 StartY=3.82843 StartZ=0 EndX=-62.3926 EndY=5.24264 EndZ=0
    g10: LineSegment StartX=-60.9784 StartY=-41.9284 StartZ=0 EndX=-62.3926 EndY=-43.3426 EndZ=0
    g11: LineSegment StartX=-60.9784 StartY=-41.9284 StartZ=0 EndX=-58.15 EndY=-39.1 EndZ=0
    g12: LineSegment StartX=-60.9784 StartY=3.82843 StartZ=0 EndX=-58.15 EndY=7 EndZ=0
    g13: LineSegment StartX=-64.15 StartY=1 StartZ=0 EndX=-60.9784 EndY=3.82843 EndZ=0
    g14: Circle CenterX=-59.5642 CenterY=2.41421 CenterZ=0 NormalX=0 NormalY=0 NormalZ=1 AngleXU=0 Radius=2
    g15: Circle CenterX=32.4142 CenterY=2.41421 CenterZ=0 NormalX=0 NormalY=0 NormalZ=1 AngleXU=0 Radius=2
    g16: Circle CenterX=32.4142 CenterY=-40.5142 CenterZ=0 NormalX=0 NormalY=0 NormalZ=1 AngleXU=0 Radius=2
    g17: Circle CenterX=-59.5642 CenterY=-40.5142 CenterZ=0 NormalX=0 NormalY=0 NormalZ=1 AngleXU=0 Radius=2
  constraints (49):
    c: Coincident(g0,g1)
    c: Coincident(g1,g2)
    c: Coincident(g2,g3)
    c: Coincident(g3,g0)
    c: Horizontal(g0)
    c: Horizontal(g2)
    c: Vertical(g1)
    c: Vertical(g3)
    c: Coincident(g4,g-13)
    c: Coincident(g4,g0)
    c: Coincident(g5,g-12)
    c: Coincident(g5,g0)
    c: Coincident(g6,g1)
    c: PointOnObject(g6,g-11)
    c: Coincident(g7,g1)
    c: Coincident(g7,g-11)
    c: Coincident(g8,g0)
    c: PointOnObject(g8,g-12)
    c: Coincident(g9,g0)
    c: PointOnObject(g9,g-13)
    c: Coincident(g10,g2)
    c: PointOnObject(g10,g-15)
    c: Coincident(g11,g2)
    c: Coincident(g11,g-15)
    c: Parallel(g11,g10)
    c: Parallel(g4,g9)
    c: Parallel(g8,g5)
    c: Parallel(g6,g7)
    c: Distance(g9) = 2
    c: Distance(g10) = 2
    c: Distance(g8) = 2
    c: Distance(g6) = 2
    c: Coincident(g12,g0)
    c: Coincident(g12,g-13)
    c: Coincident(g13,g-13)
    c: Coincident(g13,g0)
    c: Equal(g12,g13)
    c: PointOnObject(g14,g4)
    c: PointOnObject(g15,g5)
    c: PointOnObject(g16,g7)
    c: PointOnObject(g17,g11)
    c: Equal(g17,g14)
    c: Equal(g14,g15)
    c: Equal(g15,g16)
    c: Diameter(g14) = 4
    c: PointOnObject(g0,g14)
    c: PointOnObject(g2,g17)
    c: PointOnObject(g0,g15)
    c: PointOnObject(g1,g16)
FEATURE [PartDesign::Pocket] Pocket008
  BaseFeature = -> Chamfer001
  Direction = (0,0,1)
  Length = 6
  Length2 = 5
  Profile = -> Sketch018
  ReferenceAxis = -> Sketch018 [N_Axis]
  Type = 0
FEATURE [PartDesign::Body] Body001  label="ESP-Macropad-Top"
  Group = -> [Sketch011,Pad007,Sketch012,Pad008,Fillet001,Sketch013,Pocket005,Sketch014,Pocket006,Sketch015,Pocket007,Fillet002,Chamfer001,Sketch018,Pocket008]
  Origin = -> Origin001
  Tip = -> Pocket008
FEATURE [PartDesign::ShapeBinder] ShapeBinder
  Support = -> [Pocket008]
  TraceSupport = false
FEATURE [Sketcher::SketchObject] Sketch019
  ExternalGeometry = -> [ShapeBinder]
  FullyConstrained = true
  MapMode = 5
  Placement = pos=(0,0,0) rot=(0,1,0;3.14159rad)
  Support = -> [XY_Plane002]
  sketch-geometry (12):
    g0: LineSegment StartX=-31 StartY=45.1 StartZ=0 EndX=58.15 EndY=45.1 EndZ=0
    g1: ArcOfCircle CenterX=58.15 CenterY=39.1 CenterZ=0 NormalX=0 NormalY=0 NormalZ=1 AngleXU=0 Radius=6 StartAngle=2.8e-15 EndAngle=1.5708
    g2: LineSegment StartX=64.15 StartY=39.1 StartZ=0 EndX=64.15 EndY=-1.00002 EndZ=0
    g3: ArcOfCircle CenterX=58.15 CenterY=-1.00002 CenterZ=0 NormalX=0 NormalY=0 NormalZ=1 AngleXU=0 Radius=5.99998 StartAngle=4.71239 EndAngle=6.28319
    g4: LineSegment StartX=58.15 StartY=-7 StartZ=0 EndX=-31 EndY=-7 EndZ=0
    g5: ArcOfCircle CenterX=-31 CenterY=-1 CenterZ=0 NormalX=0 NormalY=0 NormalZ=1 AngleXU=0 Radius=6 StartAngle=3.14159 EndAngle=4.71239
    g6: LineSegment StartX=-37 StartY=-1 StartZ=0 EndX=-37 EndY=39.1 EndZ=0
    g7: ArcOfCircle CenterX=-31 CenterY=39.1 CenterZ=0 NormalX=0 NormalY=0 NormalZ=1 AngleXU=0 Radius=6 StartAngle=1.5708 EndAngle=3.14159
    g8: Circle CenterX=-32.4142 CenterY=40.5142 CenterZ=0 NormalX=0 NormalY=0 NormalZ=1 AngleXU=0 Radius=1.5
    g9: Circle CenterX=59.5642 CenterY=40.5142 CenterZ=0 NormalX=0 NormalY=0 NormalZ=1 AngleXU=0 Radius=1.5
    g10: Circle CenterX=59.5642 CenterY=-2.41421 CenterZ=0 NormalX=0 NormalY=0 NormalZ=1 AngleXU=0 Radius=1.5
    g11: Circle CenterX=-32.4142 CenterY=-2.41421 CenterZ=0 NormalX=0 NormalY=0 NormalZ=1 AngleXU=0 Radius=1.5
  constraints (25):
    c: Tangent(g-3,g0) = 1.5708
    c: Tangent(g0,g1) = 1.5708
    c: Coincident(g1,g-6)
    c: Coincident(g1,g2)
    c: PointOnObject(g2,g-5)
    c: Vertical(g2)
    c: Tangent(g2,g3) = 1.5708
    c: Coincident(g3,g-5)
    c: Coincident(g3,g4)
    c: Coincident(g4,g-4)
    c: Tangent(g4,g5) = 1.5708
    c: Coincident(g5,g-4)
    c: Coincident(g5,g6)
    c: Coincident(g6,g-3)
    c: Tangent(g6,g7) = 1.5708
    c: Coincident(g7,g0)
    c: Coincident(g0,g-6)
    c: Coincident(g8,g-8)
    c: Coincident(g9,g-7)
    c: Coincident(g10,g-10)
    c: Coincident(g11,g-9)
    c: Equal(g8,g11)
    c: Equal(g11,g9)
    c: Equal(g9,g10)
    c: Diameter(g8) = 3
FEATURE [PartDesign::Pad] Pad009
  Direction = (0,0,-1)
  Length = 2
  Length2 = 10
  Profile = -> Sketch019
  ReferenceAxis = -> Sketch019 [N_Axis]
  Type = 0
FEATURE [Sketcher::SketchObject] Sketch020
  ExternalGeometry = -> [ShapeBinder]
  FullyConstrained = true
  MapMode = 5
  Placement = pos=(0,0,-2) rot=(1,0,0;3.14159rad)
  Support = -> [Pad009]
  sketch-geometry (20):
    g0: LineSegment StartX=-56.65 StartY=-0.5 StartZ=0 EndX=-0.7 EndY=-0.5 EndZ=0
    g1: LineSegment StartX=-0.7 StartY=-0.5 StartZ=0 EndX=-0.7 EndY=-4.5 EndZ=0
    g2: LineSegment StartX=-0.7 StartY=-4.5 StartZ=0 EndX=-56.65 EndY=-4.5 EndZ=0
    g3: LineSegment StartX=-56.65 StartY=-4.5 StartZ=0 EndX=-56.65 EndY=-0.5 EndZ=0
    g4: LineSegment StartX=-56.65 StartY=-33.6 StartZ=0 EndX=-0.7 EndY=-33.6 EndZ=0
    g5: LineSegment StartX=-0.7 StartY=-33.6 StartZ=0 EndX=-0.7 EndY=-37.6 EndZ=0
    g6: LineSegment StartX=-0.7 StartY=-37.6 StartZ=0 EndX=-56.65 EndY=-37.6 EndZ=0
    g7: LineSegment StartX=-56.65 StartY=-37.6 StartZ=0 EndX=-56.65 EndY=-33.6 EndZ=0
    g8: LineSegment StartX=5.5 StartY=-33.6 StartZ=0 EndX=5.5 EndY=-37.6 EndZ=0
    g9: LineSegment StartX=5.5 StartY=-37.6 StartZ=0 EndX=13 EndY=-37.6 EndZ=0
    g10: LineSegment StartX=13 StartY=-37.6 StartZ=0 EndX=13 EndY=-45.1 EndZ=0
    g11: LineSegment StartX=13 StartY=-45.1 StartZ=0 EndX=24 EndY=-45.1 EndZ=0
    g12: LineSegment StartX=24 StartY=-45.1 StartZ=0 EndX=24 EndY=-37.6 EndZ=0
    g13: LineSegment StartX=24 StartY=-37.6 StartZ=0 EndX=30.5 EndY=-37.6 EndZ=0
    g14: LineSegment StartX=30.5 StartY=-37.6 StartZ=0 EndX=30.5 EndY=-33.6 EndZ=0
    g15: LineSegment StartX=30.5 StartY=-4.5 StartZ=0 EndX=30.5 EndY=-33.6 EndZ=0
    g16: LineSegment StartX=5.5 StartY=-3.5 StartZ=0 EndX=30.5 EndY=-3.5 EndZ=0
    g17: LineSegment StartX=5.5 StartY=-3.5 StartZ=0 EndX=5.5 EndY=-4.5 EndZ=0
    g18: LineSegment StartX=30.5 StartY=-3.5 StartZ=0 EndX=30.5 EndY=-4.5 EndZ=0
    g19: LineSegment StartX=5.5 StartY=-4.5 StartZ=0 EndX=5.5 EndY=-33.6 EndZ=0
  constraints (60):
    c: Coincident(g0,g1)
    c: Coincident(g1,g2)
    c: Coincident(g2,g3)
    c: Coincident(g3,g0)
    c: Horizontal(g0)
    c: Horizontal(g2)
    c: Vertical(g1)
    c: Vertical(g3)
    c: Coincident(g4,g5)
    c: Coincident(g5,g6)
    c: Coincident(g6,g7)
    c: Coincident(g7,g4)
    c: Horizontal(g4)
    c: Horizontal(g6)
    c: Vertical(g5)
    c: Vertical(g7)
    c: Equal(g3,g7)
    c: Vertical(g1,g4)
    c: Vertical(g2,g4)
    c: Horizontal(g17,g1)
    c: DistanceX(g-3,g0) = 0.5
    c: DistanceY(g-4,g6) = 0.5
    c: DistanceY(g0,g-3) = 0.5
    c: DistanceX(g1,g-5) = 0.7
    c: DistanceX(g15,g-7) = 0.5
    c: Coincident(g8,g9)
    c: Horizontal(g9)
    c: Coincident(g9,g10)
    c: Coincident(g10,g11)
    c: Horizontal(g11)
    c: Coincident(g11,g12)
    c: Coincident(g12,g13)
    c: Horizontal(g13)
    c: Coincident(g13,g14)
    c: Vertical(g8)
    c: Vertical(g14)
    c: Vertical(g12)
    c: Vertical(g10)
    c: Horizontal(g8,g4)
    c: Horizontal(g8,g5)
    c: Vertical(g14,g15)
    c: Horizontal(g9,g12)
    c: Horizontal(g10,g-8)
    c: DistanceX(g-8,g10) = 0.5
    c: DistanceX(g11,g-9) = 0.5
    c: DistanceX(g-6,g8) = 0.5
    c: DistanceY(g5,g5) = 4
    c: Coincident(g15,g14)
    c: Horizontal(g15,g17)
    c: Horizontal(g14,g8)
    c: Horizontal(g16)
    c: Coincident(g17,g16)
    c: Coincident(g18,g16)
    c: Coincident(g18,g15)
    c: Vertical(g18)
    c: Vertical(g17)
    c: DistanceY(g16,g-7) = 0.5
    c: Vertical(g8,g17)
    c: Coincident(g19,g17)
    c: Coincident(g19,g8)
FEATURE [PartDesign::Pad] Pad010
  BaseFeature = -> Pad009
  Direction = (0,0,-1)
  Length = 1
  Length2 = 10
  Profile = -> Sketch020
  ReferenceAxis = -> Sketch020 [N_Axis]
  Type = 0
FEATURE [PartDesign::Chamfer] Chamfer002
  Angle = 45
  Base = -> Pad010 [Edge19,Edge20,Edge21,Edge18]
  BaseFeature = -> Pad010
  ChamferType = 0
  FlipDirection = false
  Size = 1
  Size2 = 1
  SupportTransform = false
  UseAllEdges = false
FEATURE [PartDesign::Body] Body002  label="ESP-Macropad-Bottom"
  Group = -> [Sketch019,ShapeBinder,Pad009,Sketch020,Pad010,Chamfer002]
  Origin = -> Origin002
  Tip = -> Chamfer002
FEATURE [Part::Mirroring] Part__Mirroring  label="ESP-Macropad-Bottom (Mirror #1)"
  Base = (0,0,0)
  Normal = (0,0,1)
  Source = -> Body002
FEATURE [TechDraw::DrawSVGTemplate] Template
  EditableTexts = Designed_by_Name=<owner>; Drawing_number=1; FC-Date=2023-12-06; FC-SC=1:1; FC-SH=1; FC-Title=Macropad; Subtitle=Wemos D1 Mini based 6-Key Macropad; Weight=n/a
  Height = 210
  Orientation = 1
  Template = /nix/store/29d0l5zyj8xhlz06ml5gbz9jzk7y3hfr-freecad-0.21.2/share/Mod/TechDraw/Templates/A4_LandscapeTD.svg
  Width = 297
FEATURE [TechDraw::DrawViewPart] View
  CoarseView = false
  Direction = (0,0,-1)
  Focus = 100
  HardHidden = false
  IsoCount = 0
  IsoHidden = false
  IsoVisible = false
  LockPosition = false
  Perspective = false
  Rotation = 0
  ScaleType = 0
  ScrubCount = 0
  SeamHidden = false
  SeamVisible = false
  SmoothHidden = false
  SmoothVisible = true
  Source = -> [Body001]
  X = 72.5856
  XDirection = (1,0,0)
  Y = 62.5508
FEATURE [TechDraw::DrawViewPart] View002
  CoarseView = false
  Direction = (0,0,1)
  Focus = 100
  HardHidden = false
  IsoCount = 0
  IsoHidden = false
  IsoVisible = false
  LockPosition = false
  Perspective = false
  Rotation = 0
  ScaleType = 0
  ScrubCount = 0
  SeamHidden = false
  SeamVisible = false
  SmoothHidden = false
  SmoothVisible = true
  Source = -> [Body001]
  X = 72.5856
  XDirection = (-1,0,0)
  Y = 164.294
FEATURE [TechDraw::DrawViewPart] View003
  CoarseView = false
  Direction = (-0.5,-0.5,0.707107)
  Focus = 100
  HardHidden = false
  IsoCount = 0
  IsoHidden = false
  IsoVisible = false
  LockPosition = false
  Perspective = false
  Rotation = 0
  Scale = 0.7
  ScaleType = 2
  ScrubCount = 0
  SeamHidden = false
  SeamVisible = false
  SmoothHidden = false
  SmoothVisible = true
  Source = -> [Body001]
  X = 178.596
  XDirection = (0.707107,-0.707107,0)
  Y = 164.519
FEATURE [TechDraw::DrawViewPart] View004
  CoarseView = false
  Direction = (-0.5,-0.5,0.707107)
  Focus = 100
  HardHidden = false
  IsoCount = 0
  IsoHidden = false
  IsoVisible = false
  LockPosition = false
  Perspective = false
  Rotation = 0
  Scale = 0.7
  ScaleType = 2
  ScrubCount = 0
  SeamHidden = false
  SeamVisible = false
  SmoothHidden = false
  SmoothVisible = true
  Source = -> [Part__Mirroring]
  X = 246.65
  XDirection = (0.707107,-0.707107,0)
  Y = 162.947
FEATURE [TechDraw::DrawViewDimension] Dimension
  AngleOverride = false
  Arbitrary = false
  ArbitraryTolerances = false
  EqualTolerance = true
  ExtensionAngle = 0
  FormatSpec = %.2w
  FormatSpecOverTolerance = %+.2w
  FormatSpecUnderTolerance = %+.2w
  Inverted = false
  LineAngle = 0
  LockPosition = false
  MeasureType = 1
  OverTolerance = 0
  References2D = -> [View002]
  Rotation = 0
  ScaleType = 0
  TheoreticalExact = false
  Type = 0
  UnderTolerance = 0
  X = -29.8717
  Y = -28.1061
FEATURE [TechDraw::DrawViewDimension] Dimension001
  AngleOverride = false
  Arbitrary = false
  ArbitraryTolerances = false
  EqualTolerance = true
  ExtensionAngle = 0
  FormatSpec = %.2w
  FormatSpecOverTolerance = %+.2w
  FormatSpecUnderTolerance = %+.2w
  Inverted = false
  LineAngle = 0
  LockPosition = false
  MeasureType = 1
  OverTolerance = 0
  References2D = -> [View]
  Rotation = 0
  ScaleType = 0
  TheoreticalExact = false
  Type = 1
  UnderTolerance = 0
  X = 32.0242
  Y = 41.4591
FEATURE [TechDraw::DrawViewDimension] Dimension002
  AngleOverride = false
  Arbitrary = false
  ArbitraryTolerances = false
  EqualTolerance = true
  ExtensionAngle = 0
  FormatSpec = %.2w
  FormatSpecOverTolerance = %+.2w
  FormatSpecUnderTolerance = %+.2w
  Inverted = false
  LineAngle = 0
  LockPosition = false
  MeasureType = 1
  OverTolerance = 0
  References2D = -> [View]
  Rotation = 0
  ScaleType = 0
  TheoreticalExact = false
  Type = 2
  UnderTolerance = 0
  X = 61.1953
  Y = 2.34759
FEATURE [TechDraw::DrawViewDimension] Dimension003
  AngleOverride = false
  Arbitrary = false
  ArbitraryTolerances = false
  EqualTolerance = true
  ExtensionAngle = 0
  FormatSpec = %.2w
  FormatSpecOverTolerance = %+.2w
  FormatSpecUnderTolerance = %+.2w
  Inverted = false
  LineAngle = 0
  LockPosition = false
  MeasureType = 1
  OverTolerance = 0
  References2D = -> [View]
  Rotation = 0
  ScaleType = 0
  TheoreticalExact = false
  Type = 1
  UnderTolerance = 0
  X = 55.2501
  Y = -30.9243
FEATURE [TechDraw::DrawViewDimension] Dimension004
  AngleOverride = false
  Arbitrary = false
  ArbitraryTolerances = false
  EqualTolerance = true
  ExtensionAngle = 0
  FormatSpec = %.2w
  FormatSpecOverTolerance = %+.2w
  FormatSpecUnderTolerance = %+.2w
  Inverted = false
  LineAngle = 0
  LockPosition = false
  MeasureType = 1
  OverTolerance = 0
  References2D = -> [View]
  Rotation = 0
  ScaleType = 0
  TheoreticalExact = false
  Type = 1
  UnderTolerance = 0
  X = 9.97206
  Y = -30.9243
FEATURE [TechDraw::DrawViewDimension] Dimension005
  AngleOverride = false
  Arbitrary = false
  ArbitraryTolerances = false
  EqualTolerance = true
  ExtensionAngle = 0
  FormatSpec = %.2w
  FormatSpecOverTolerance = %+.2w
  FormatSpecUnderTolerance = %+.2w
  Inverted = false
  LineAngle = 0
  LockPosition = false
  MeasureType = 1
  OverTolerance = 0
  References2D = -> [View002]
  Rotation = 0
  ScaleType = 0
  TheoreticalExact = false
  Type = 2
  UnderTolerance = 0
  X = 60.5215
  Y = 2.0508
FEATURE [TechDraw::DrawViewDimension] Dimension006
  AngleOverride = false
  Arbitrary = false
  ArbitraryTolerances = false
  EqualTolerance = true
  ExtensionAngle = 0
  FormatSpec = %.2w
  FormatSpecOverTolerance = %+.2w
  FormatSpecUnderTolerance = %+.2w
  Inverted = false
  LineAngle = 0
  LockPosition = false
  MeasureType = 1
  OverTolerance = 0
  References2D = -> [View002]
  Rotation = 0
  ScaleType = 0
  TheoreticalExact = false
  Type = 1
  UnderTolerance = 0
  X = 15.4492
  Y = -39.0099
FEATURE [TechDraw::DrawViewDimension] Dimension007
  AngleOverride = false
  Arbitrary = false
  ArbitraryTolerances = false
  EqualTolerance = true
  ExtensionAngle = 0
  FormatSpec = %.2w
  FormatSpecOverTolerance = %+.2w
  FormatSpecUnderTolerance = %+.2w
  Inverted = false
  LineAngle = 0
  LockPosition = false
  MeasureType = 1
  OverTolerance = 0
  References2D = -> [View]
  Rotation = 0
  ScaleType = 0
  TheoreticalExact = false
  Type = 1
  UnderTolerance = 0
  X = -34.7221
  Y = 42.2639
FEATURE [TechDraw::DrawViewDimension] Dimension008
  AngleOverride = false
  Arbitrary = false
  ArbitraryTolerances = false
  EqualTolerance = true
  ExtensionAngle = 0
  FormatSpec = %.2w
  FormatSpecOverTolerance = %+.2w
  FormatSpecUnderTolerance = %+.2w
  Inverted = false
  LineAngle = 0
  LockPosition = false
  MeasureType = 1
  OverTolerance = 0
  References2D = -> [View]
  Rotation = 0
  ScaleType = 0
  TheoreticalExact = false
  Type = 1
  UnderTolerance = 0
  X = 31.8504
  Y = -2.40027
FEATURE [TechDraw::DrawViewDimension] Dimension009
  AngleOverride = false
  Arbitrary = false
  ArbitraryTolerances = false
  EqualTolerance = true
  ExtensionAngle = 0
  FormatSpec = ⌀%.2w
  FormatSpecOverTolerance = %+.2w
  FormatSpecUnderTolerance = %+.2w
  Inverted = false
  LineAngle = 0
  LockPosition = false
  MeasureType = 1
  OverTolerance = 0
  References2D = -> [View]
  Rotation = 0
  ScaleType = 0
  TheoreticalExact = false
  Type = 5
  UnderTolerance = 0
  X = 56.3743
  Y = 37.508
FEATURE [TechDraw::DrawViewPart] View005
  CoarseView = false
  Direction = (0,1,0)
  Focus = 100
  HardHidden = false
  IsoCount = 0
  IsoHidden = false
  IsoVisible = false
  LockPosition = false
  Perspective = false
  Rotation = 0
  ScaleType = 0
  ScrubCount = 0
  SeamHidden = false
  SeamVisible = false
  SmoothHidden = false
  SmoothVisible = true
  Source = -> [Part__Mirroring]
  X = 193.869
  XDirection = (-1,0,0)
  Y = 73.7807
FEATURE [TechDraw::DrawViewPart] View006
  CoarseView = false
  Direction = (0,1,0)
  Focus = 100
  HardHidden = false
  IsoCount = 0
  IsoHidden = false
  IsoVisible = false
  LockPosition = false
  Perspective = false
  Rotation = 0
  ScaleType = 0
  ScrubCount = 0
  SeamHidden = false
  SeamVisible = false
  SmoothHidden = false
  SmoothVisible = true
  Source = -> [Body001]
  X = 193.869
  XDirection = (-1,0,0)
  Y = 110.39
FEATURE [TechDraw::DrawViewDimension] Dimension010
  AngleOverride = false
  Arbitrary = false
  ArbitraryTolerances = false
  EqualTolerance = true
  ExtensionAngle = 0
  FormatSpec = %.2w
  FormatSpecOverTolerance = %+.2w
  FormatSpecUnderTolerance = %+.2w
  Inverted = false
  LineAngle = 0
  LockPosition = false
  MeasureType = 1
  OverTolerance = 0
  References2D = -> [View006]
  Rotation = 0
  ScaleType = 0
  TheoreticalExact = false
  Type = 2
  UnderTolerance = 0
  X = 56.5591
  Y = 21.6081
FEATURE [TechDraw::DrawViewDimension] Dimension011
  AngleOverride = false
  Arbitrary = false
  ArbitraryTolerances = false
  EqualTolerance = true
  ExtensionAngle = 0
  FormatSpec = %.2w
  FormatSpecOverTolerance = %+.2w
  FormatSpecUnderTolerance = %+.2w
  Inverted = false
  LineAngle = 0
  LockPosition = false
  MeasureType = 1
  OverTolerance = 0
  References2D = -> [View005]
  Rotation = 0
  ScaleType = 0
  TheoreticalExact = false
  Type = 2
  UnderTolerance = 0
  X = 56.3517
  Y = -3.86698
FEATURE [TechDraw::DrawViewDimension] Dimension012
  AngleOverride = false
  Arbitrary = false
  ArbitraryTolerances = false
  EqualTolerance = true
  ExtensionAngle = 0
  FormatSpec = %.2w
  FormatSpecOverTolerance = %+.2w
  FormatSpecUnderTolerance = %+.2w
  Inverted = false
  LineAngle = 0
  LockPosition = false
  MeasureType = 1
  OverTolerance = 0
  References2D = -> [View005]
  Rotation = 0
  ScaleType = 0
  TheoreticalExact = false
  Type = 2
  UnderTolerance = 0
  X = 61.398
  Y = 12.9774
FEATURE [TechDraw::DrawViewDimension] Dimension013
  AngleOverride = false
  Arbitrary = false
  ArbitraryTolerances = false
  EqualTolerance = true
  ExtensionAngle = 0
  FormatSpec = %.2w
  FormatSpecOverTolerance = %+.2w
  FormatSpecUnderTolerance = %+.2w
  Inverted = false
  LineAngle = 0
  LockPosition = false
  MeasureType = 1
  OverTolerance = 0
  References2D = -> [View005]
  Rotation = 0
  ScaleType = 0
  TheoreticalExact = false
  Type = 1
  UnderTolerance = 0
  X = -32.2802
  Y = 13.1672
FEATURE [TechDraw::DrawViewDimension] Dimension014
  AngleOverride = false
  Arbitrary = false
  ArbitraryTolerances = false
  EqualTolerance = true
  ExtensionAngle = 0
  FormatSpec = %.2w
  FormatSpecOverTolerance = %+.2w
  FormatSpecUnderTolerance = %+.2w
  Inverted = false
  LineAngle = 0
  LockPosition = false
  MeasureType = 1
  OverTolerance = 0
  References2D = -> [View006]
  Rotation = 0
  ScaleType = 0
  TheoreticalExact = false
  Type = 1
  UnderTolerance = 0
  X = -32.4981
  Y = -11.2182
FEATURE [TechDraw::DrawViewDimension] Dimension015
  AngleOverride = false
  Arbitrary = false
  ArbitraryTolerances = false
  EqualTolerance = true
  ExtensionAngle = 0
  FormatSpec = %.2w
  FormatSpecOverTolerance = %+.2w
  FormatSpecUnderTolerance = %+.2w
  Inverted = false
  LineAngle = 0
  LockPosition = false
  MeasureType = 1
  OverTolerance = 0
  References2D = -> [View006]
  Rotation = 0
  ScaleType = 0
  TheoreticalExact = false
  Type = 2
  UnderTolerance = 0
  X = -18.3951
  Y = 3.8465
FEATURE [TechDraw::DrawViewDimension] Dimension016
  AngleOverride = false
  Arbitrary = false
  ArbitraryTolerances = false
  EqualTolerance = true
  ExtensionAngle = 0
  FormatSpec = %.2w
  FormatSpecOverTolerance = %+.2w
  FormatSpecUnderTolerance = %+.2w
  Inverted = false
  LineAngle = 0
  LockPosition = false
  MeasureType = 1
  OverTolerance = 0
  References2D = -> [View]
  Rotation = 0
  ScaleType = 0
  TheoreticalExact = false
  Type = 2
  UnderTolerance = 0
  X = -35.5891
  Y = 11.4741
FEATURE [TechDraw::DrawViewDimension] Dimension017
  AngleOverride = false
  Arbitrary = false
  ArbitraryTolerances = false
  EqualTolerance = true
  ExtensionAngle = 0
  FormatSpec = R%.2w
  FormatSpecOverTolerance = %+.2w
  FormatSpecUnderTolerance = %+.2w
  Inverted = false
  LineAngle = 0
  LockPosition = false
  MeasureType = 1
  OverTolerance = 0
  References2D = -> [View002]
  Rotation = 0
  ScaleType = 0
  TheoreticalExact = false
  Type = 4
  UnderTolerance = 0
  X = -33.3301
  Y = 20.1083
FEATURE [TechDraw::DrawPage] Page
  KeepUpdated = true
  NextBalloonIndex = 1
  ProjectionType = 0
  Template = -> Template
  Views = -> [View,View002,View003,View004,Dimension,Dimension001,Dimension002,Dimension003,Dimension004,Dimension005,Dimension006,Dimension007,Dimension008,Dimension009,View005,View006,Dimension010,Dimension011,Dimension012,Dimension013,Dimension014,Dimension015,Dimension016,Dimension017]
